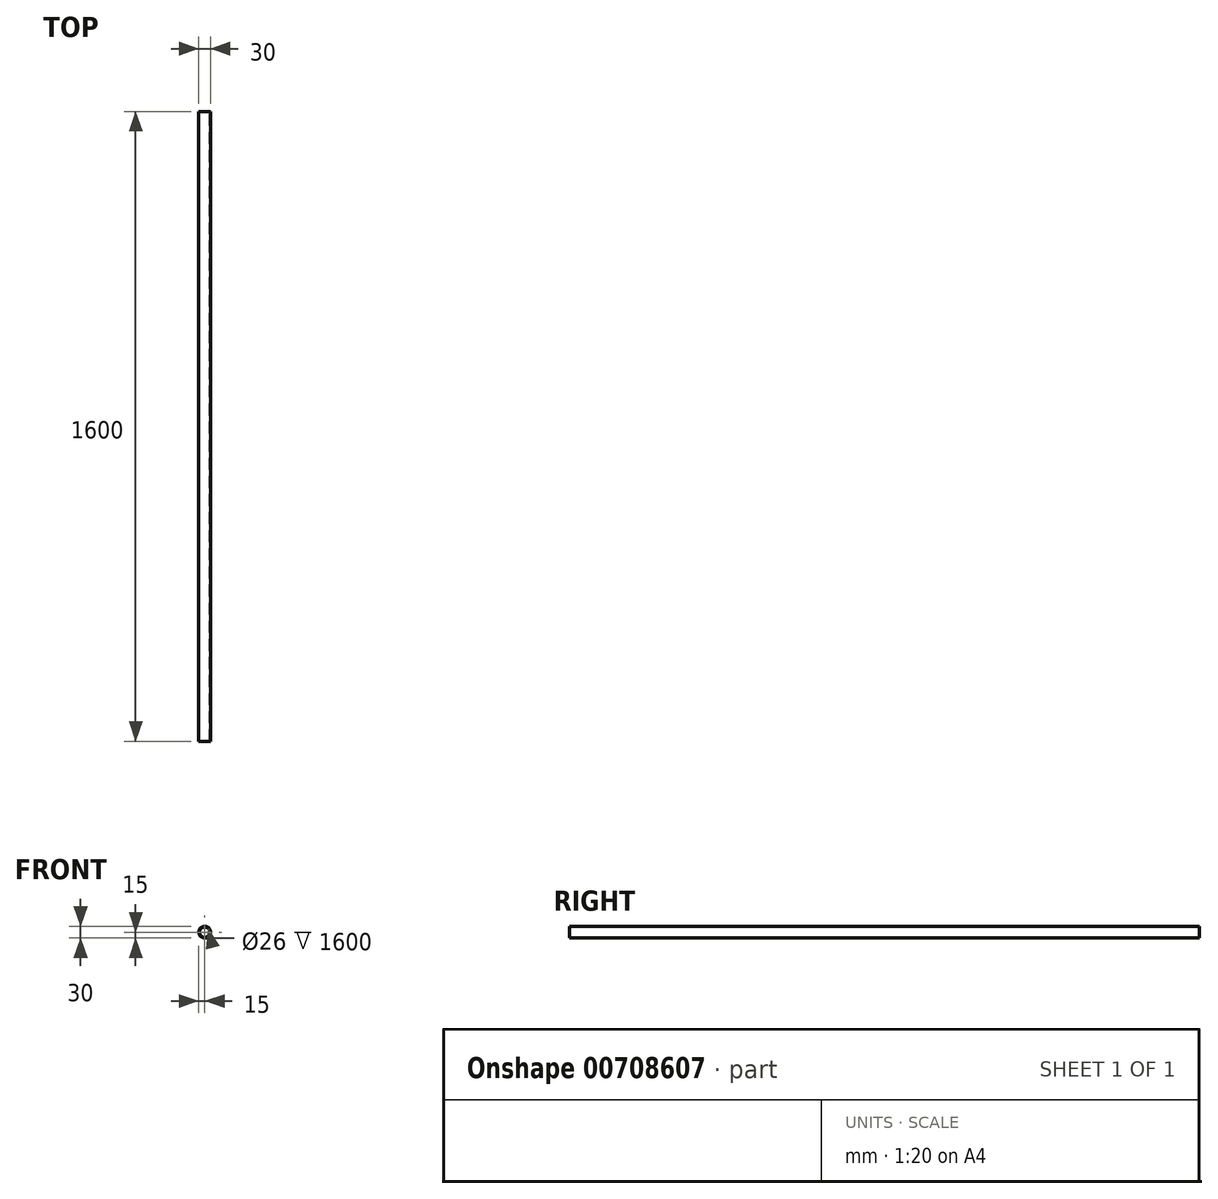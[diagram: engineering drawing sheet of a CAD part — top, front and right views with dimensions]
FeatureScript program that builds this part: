
annotation { "Feature Type Name" : "Feature", "Feature Type Description" : "" }
export const myFeature = defineFeature(function(context is Context, id is Id, definition is map)
    precondition{}
    {
        {
            var Q0;
            Q0=qCreatedBy(makeId("Front.planeOp"),FACE);
            var sketch = newSketch(context, id + "F0", { "sketchPlane" : qUnion([Q0])});
            skCircle(sketch, "E0", {"center": v(0, 0) * mm, "radius": 15 * mm});
            skCircle(sketch, "E1", {"center": v(0, 0) * mm, "radius": 13 * mm});
            skSolve(sketch);
        }
        {
            var Q0;
            Q0=makeQuery(id+"F0.imprint","IMPRINT",FACE,{"disambiguationData":[TD([[makeQuery(id+"F0.imprint","IMPRINT",EDGE,{"derivedFrom":sQuery(id+"F0.wireOp",EDGE,"E0")}),1.0]])]});
            extrude(context, id + "F1", {"entities" : qUnion([Q0]), "depth" : 1600 * mm, "offsetDistance" : 25 * mm});
        }
    });
